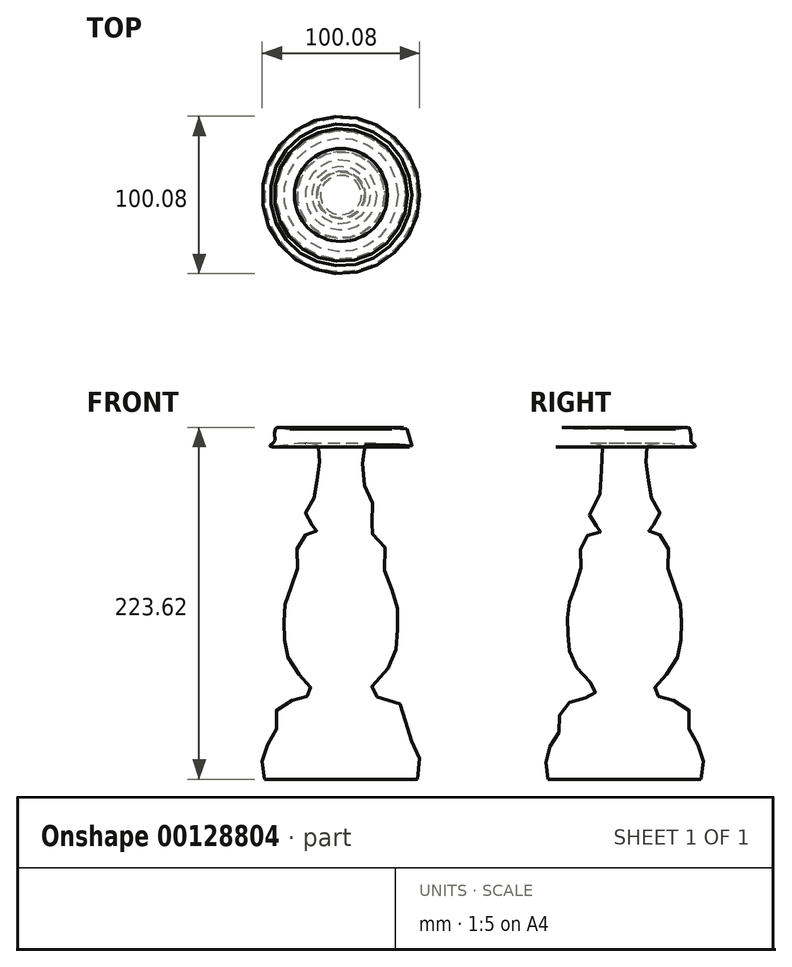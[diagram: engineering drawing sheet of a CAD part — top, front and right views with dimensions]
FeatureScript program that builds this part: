
annotation { "Feature Type Name" : "Feature", "Feature Type Description" : "" }
export const myFeature = defineFeature(function(context is Context, id is Id, definition is map)
    precondition{}
    {
        {
            var Q0;
            Q0=qCreatedBy(makeId("Top.planeOp"),FACE);
            cPlane(context, id + "F0", {"entities" : qUnion([Q0]), "cplaneType" : CPlaneType.OFFSET, "offset" : 19 * mm, "width" : 150 * mm, "height" : 150 * mm});
        }
        {
            var Q0;
            Q0=qCreatedBy(id+"F0.planeOp",FACE);
            cPlane(context, id + "F1", {"entities" : qUnion([Q0]), "cplaneType" : CPlaneType.OFFSET, "offset" : 3 * mm, "width" : 150 * mm, "height" : 150 * mm});
        }
        {
            var Q0;
            Q0=qCreatedBy(id+"F1.planeOp",FACE);
            cPlane(context, id + "F2", {"entities" : qUnion([Q0]), "cplaneType" : CPlaneType.OFFSET, "offset" : 5 * mm, "width" : 150 * mm, "height" : 150 * mm});
        }
        {
            var Q0;
            Q0=qCreatedBy(id+"F2.planeOp",FACE);
            cPlane(context, id + "F3", {"entities" : qUnion([Q0]), "cplaneType" : CPlaneType.OFFSET, "offset" : 5 * mm, "width" : 150 * mm, "height" : 150 * mm});
        }
        {
            var Q0;
            Q0=qCreatedBy(id+"F3.planeOp",FACE);
            cPlane(context, id + "F4", {"entities" : qUnion([Q0]), "cplaneType" : CPlaneType.OFFSET, "offset" : 13 * mm, "width" : 150 * mm, "height" : 150 * mm});
        }
        {
            var Q0;
            Q0=qCreatedBy(id+"F4.planeOp",FACE);
            cPlane(context, id + "F5", {"entities" : qUnion([Q0]), "cplaneType" : CPlaneType.OFFSET, "offset" : 10 * mm, "width" : 150 * mm, "height" : 150 * mm});
        }
        {
            var Q0;
            Q0=qCreatedBy(id+"F5.planeOp",FACE);
            cPlane(context, id + "F6", {"entities" : qUnion([Q0]), "cplaneType" : CPlaneType.OFFSET, "offset" : 15 * mm, "width" : 150 * mm, "height" : 150 * mm});
        }
        {
            var Q0;
            Q0=qCreatedBy(id+"F6.planeOp",FACE);
            cPlane(context, id + "F7", {"entities" : qUnion([Q0]), "cplaneType" : CPlaneType.OFFSET, "offset" : 25 * mm, "width" : 150 * mm, "height" : 150 * mm});
        }
        {
            var Q0;
            Q0=qCreatedBy(id+"F7.planeOp",FACE);
            cPlane(context, id + "F8", {"entities" : qUnion([Q0]), "cplaneType" : CPlaneType.OFFSET, "offset" : 20 * mm, "width" : 150 * mm, "height" : 150 * mm});
        }
        {
            var Q0;
            Q0=qCreatedBy(id+"F8.planeOp",FACE);
            cPlane(context, id + "F9", {"entities" : qUnion([Q0]), "cplaneType" : CPlaneType.OFFSET, "offset" : 20 * mm, "width" : 150 * mm, "height" : 150 * mm});
        }
        {
            var Q0;
            Q0=qCreatedBy(id+"F9.planeOp",FACE);
            cPlane(context, id + "F10", {"entities" : qUnion([Q0]), "cplaneType" : CPlaneType.OFFSET, "offset" : 20 * mm, "width" : 150 * mm, "height" : 150 * mm});
        }
        {
            var Q0;
            Q0=qCreatedBy(id+"F10.planeOp",FACE);
            cPlane(context, id + "F11", {"entities" : qUnion([Q0]), "cplaneType" : CPlaneType.OFFSET, "offset" : 2 * mm, "width" : 150 * mm, "height" : 150 * mm});
        }
        {
            var Q0;
            Q0=qCreatedBy(id+"F11.planeOp",FACE);
            cPlane(context, id + "F12", {"entities" : qUnion([Q0]), "cplaneType" : CPlaneType.OFFSET, "offset" : 8.5 * mm, "width" : 150 * mm, "height" : 150 * mm});
        }
        {
            var Q0;
            Q0=qCreatedBy(id+"F12.planeOp",FACE);
            cPlane(context, id + "F13", {"entities" : qUnion([Q0]), "cplaneType" : CPlaneType.OFFSET, "offset" : 8.5 * mm, "width" : 150 * mm, "height" : 150 * mm});
        }
        {
            var Q0;
            Q0=qCreatedBy(id+"F13.planeOp",FACE);
            cPlane(context, id + "F14", {"entities" : qUnion([Q0]), "cplaneType" : CPlaneType.OFFSET, "offset" : 8.5 * mm, "width" : 150 * mm, "height" : 150 * mm});
        }
        {
            var Q0;
            Q0=qCreatedBy(id+"F14.planeOp",FACE);
            cPlane(context, id + "F15", {"entities" : qUnion([Q0]), "cplaneType" : CPlaneType.OFFSET, "offset" : 8.5 * mm, "width" : 150 * mm, "height" : 150 * mm});
        }
        {
            var Q0;
            Q0=qCreatedBy(id+"F15.planeOp",FACE);
            cPlane(context, id + "F16", {"entities" : qUnion([Q0]), "cplaneType" : CPlaneType.OFFSET, "offset" : 1 * mm, "width" : 150 * mm, "height" : 150 * mm});
        }
        {
            var Q0;
            Q0=qCreatedBy(id+"F16.planeOp",FACE);
            cPlane(context, id + "F17", {"entities" : qUnion([Q0]), "cplaneType" : CPlaneType.OFFSET, "offset" : 20 * mm, "width" : 150 * mm, "height" : 150 * mm});
        }
        {
            var Q0;
            Q0=qCreatedBy(id+"F17.planeOp",FACE);
            cPlane(context, id + "F18", {"entities" : qUnion([Q0]), "cplaneType" : CPlaneType.OFFSET, "offset" : 1 * mm, "width" : 150 * mm, "height" : 150 * mm});
        }
        {
            var Q0;
            Q0=qCreatedBy(id+"F18.planeOp",FACE);
            cPlane(context, id + "F19", {"entities" : qUnion([Q0]), "cplaneType" : CPlaneType.OFFSET, "offset" : 2 * mm, "width" : 150 * mm, "height" : 150 * mm});
        }
        {
            var Q0;
            Q0=qCreatedBy(id+"F19.planeOp",FACE);
            cPlane(context, id + "F20", {"entities" : qUnion([Q0]), "cplaneType" : CPlaneType.OFFSET, "offset" : 3 * mm, "width" : 150 * mm, "height" : 150 * mm});
        }
        {
            var Q0;
            Q0=qCreatedBy(id+"F20.planeOp",FACE);
            cPlane(context, id + "F21", {"entities" : qUnion([Q0]), "cplaneType" : CPlaneType.OFFSET, "offset" : 2 * mm, "width" : 150 * mm, "height" : 150 * mm});
        }
        {
            var Q0;
            Q0=qCreatedBy(id+"F21.planeOp",FACE);
            cPlane(context, id + "F22", {"entities" : qUnion([Q0]), "cplaneType" : CPlaneType.OFFSET, "offset" : 3 * mm, "width" : 150 * mm, "height" : 150 * mm});
        }
        {
            var Q0;
            Q0=qCreatedBy(id+"F22.planeOp",FACE);
            cPlane(context, id + "F23", {"entities" : qUnion([Q0]), "cplaneType" : CPlaneType.OFFSET, "offset" : 0.4 * mm, "width" : 150 * mm, "height" : 150 * mm});
        }
        {
            var Q0;
            Q0=qCreatedBy(makeId("Top.planeOp"),FACE);
            var sketch = newSketch(context, id + "F24", { "sketchPlane" : qUnion([Q0])});
            skCircle(sketch, "E0", {"center": v(0, 0) * mm, "radius": 48.5 * mm});
            skSolve(sketch);
        }
        {
            var Q0;
            Q0=qCreatedBy(id+"F0.planeOp",FACE);
            var sketch = newSketch(context, id + "F25", { "sketchPlane" : qUnion([Q0])});
            skCircle(sketch, "E1", {"center": v(0, 0) * mm, "radius": 48.5 * mm});
            skSolve(sketch);
        }
        {
            var Q0;
            Q0=qCreatedBy(id+"F2.planeOp",FACE);
            var sketch = newSketch(context, id + "F26", { "sketchPlane" : qUnion([Q0])});
            skCircle(sketch, "E2", {"center": v(0, 0) * mm, "radius": 43 * mm});
            skSolve(sketch);
        }
        {
            var Q0;
            Q0=qCreatedBy(id+"F3.planeOp",FACE);
            var sketch = newSketch(context, id + "F27", { "sketchPlane" : qUnion([Q0])});
            skCircle(sketch, "E3", {"center": v(0, 0) * mm, "radius": 41 * mm});
            skSolve(sketch);
        }
        {
            var Q0;
            Q0=qCreatedBy(id+"F4.planeOp",FACE);
            var sketch = newSketch(context, id + "F28", { "sketchPlane" : qUnion([Q0])});
            skCircle(sketch, "E4", {"center": v(0, 0) * mm, "radius": 40.5 * mm});
            skSolve(sketch);
        }
        {
            var Q0;
            Q0=qCreatedBy(id+"F5.planeOp",FACE);
            var sketch = newSketch(context, id + "F29", { "sketchPlane" : qUnion([Q0])});
            skCircle(sketch, "E5", {"center": v(0, 0) * mm, "radius": 18.5 * mm});
            skSolve(sketch);
        }
        {
            var Q0;
            Q0=qCreatedBy(id+"F6.planeOp",FACE);
            var sketch = newSketch(context, id + "F30", { "sketchPlane" : qUnion([Q0])});
            skCircle(sketch, "E6", {"center": v(0, 0) * mm, "radius": 29.5 * mm});
            skSolve(sketch);
        }
        {
            var Q0;
            Q0=qCreatedBy(id+"F7.planeOp",FACE);
            var sketch = newSketch(context, id + "F31", { "sketchPlane" : qUnion([Q0])});
            skCircle(sketch, "E7", {"center": v(0, 0) * mm, "radius": 36 * mm});
            skSolve(sketch);
        }
        {
            var Q0;
            Q0=qCreatedBy(id+"F8.planeOp",FACE);
            var sketch = newSketch(context, id + "F32", { "sketchPlane" : qUnion([Q0])});
            skCircle(sketch, "E8", {"center": v(0, 0) * mm, "radius": 34.5 * mm});
            skSolve(sketch);
        }
        {
            var Q0;
            Q0=qCreatedBy(id+"F9.planeOp",FACE);
            var sketch = newSketch(context, id + "F33", { "sketchPlane" : qUnion([Q0])});
            skCircle(sketch, "E9", {"center": v(0, 0) * mm, "radius": 27.5 * mm});
            skSolve(sketch);
        }
        {
            var Q0;
            Q0=qCreatedBy(id+"F10.planeOp",FACE);
            var sketch = newSketch(context, id + "F34", { "sketchPlane" : qUnion([Q0])});
            skCircle(sketch, "E10", {"center": v(0, 0) * mm, "radius": 23.5 * mm});
            skSolve(sketch);
        }
        {
            var Q0;
            Q0=qCreatedBy(id+"F11.planeOp",FACE);
            var sketch = newSketch(context, id + "F35", { "sketchPlane" : qUnion([Q0])});
            skCircle(sketch, "E11", {"center": v(0, 0) * mm, "radius": 15.5 * mm});
            skSolve(sketch);
        }
        {
            var Q0;
            Q0=qCreatedBy(id+"F12.planeOp",FACE);
            var sketch = newSketch(context, id + "F36", { "sketchPlane" : qUnion([Q0])});
            skCircle(sketch, "E12", {"center": v(0, 0) * mm, "radius": 21.5 * mm});
            skSolve(sketch);
        }
        {
            var Q0;
            Q0=qCreatedBy(id+"F13.planeOp",FACE);
            var sketch = newSketch(context, id + "F37", { "sketchPlane" : qUnion([Q0])});
            skCircle(sketch, "E13", {"center": v(0, 0) * mm, "radius": 21.04 * mm});
            skSolve(sketch);
        }
        {
            var Q0;
            Q0=qCreatedBy(id+"F14.planeOp",FACE);
            var sketch = newSketch(context, id + "F38", { "sketchPlane" : qUnion([Q0])});
            skCircle(sketch, "E14", {"center": v(0, 0) * mm, "radius": 15 * mm});
            skSolve(sketch);
        }
        {
            var Q0;
            Q0=qCreatedBy(id+"F15.planeOp",FACE);
            var sketch = newSketch(context, id + "F39", { "sketchPlane" : qUnion([Q0])});
            skCircle(sketch, "E15", {"center": v(0, 0) * mm, "radius": 15.25 * mm});
            skSolve(sketch);
        }
        {
            var Q0;
            Q0=qCreatedBy(id+"F16.planeOp",FACE);
            var sketch = newSketch(context, id + "F40", { "sketchPlane" : qUnion([Q0])});
            skCircle(sketch, "E16", {"center": v(0, 0) * mm, "radius": 15.25 * mm});
            skSolve(sketch);
        }
        {
            var Q0;
            Q0=qCreatedBy(id+"F17.planeOp",FACE);
            var sketch = newSketch(context, id + "F41", { "sketchPlane" : qUnion([Q0])});
            skCircle(sketch, "E17", {"center": v(0, 0) * mm, "radius": 15 * mm});
            skSolve(sketch);
        }
        {
            var Q0;
            Q0=qCreatedBy(id+"F18.planeOp",FACE);
            var sketch = newSketch(context, id + "F42", { "sketchPlane" : qUnion([Q0])});
            skCircle(sketch, "E18", {"center": v(0, 0) * mm, "radius": 44 * mm});
            skSolve(sketch);
        }
        {
            var Q0;
            Q0=qCreatedBy(id+"F19.planeOp",FACE);
            var sketch = newSketch(context, id + "F43", { "sketchPlane" : qUnion([Q0])});
            skCircle(sketch, "E19", {"center": v(0, 0) * mm, "radius": 42 * mm});
            skSolve(sketch);
        }
        {
            var Q0;
            Q0=qCreatedBy(id+"F20.planeOp",FACE);
            var sketch = newSketch(context, id + "F44", { "sketchPlane" : qUnion([Q0])});
            skCircle(sketch, "E20", {"center": v(0, 0) * mm, "radius": 42 * mm});
            skSolve(sketch);
        }
        {
            var Q0;
            Q0=qCreatedBy(id+"F22.planeOp",FACE);
            var sketch = newSketch(context, id + "F45", { "sketchPlane" : qUnion([Q0])});
            skCircle(sketch, "E21", {"center": v(0, 0) * mm, "radius": 41.5 * mm});
            skSolve(sketch);
        }
        {
            var Q0;
            Q0=qCreatedBy(id+"F22.planeOp",FACE);
            var sketch = newSketch(context, id + "F46", { "sketchPlane" : qUnion([Q0])});
            skCircle(sketch, "E22", {"center": v(0, 0) * mm, "radius": 30 * mm});
            skSolve(sketch);
        }
        {
            var Q0;
            Q0=qCreatedBy(id+"F23.planeOp",FACE);
            var sketch = newSketch(context, id + "F47", { "sketchPlane" : qUnion([Q0])});
            skCircle(sketch, "E23", {"center": v(0, 0) * mm, "radius": 29.5 * mm});
            skSolve(sketch);
        }
        {
            var Q0;
            Q0 = qSketchRegion(id + "F24", true);
            var Q1;
            Q1 = qSketchRegion(id + "F25", true);
            var Q2;
            Q2 = qSketchRegion(id + "F26", true);
            var Q3;
            Q3 = qSketchRegion(id + "F27", true);
            var Q4;
            Q4 = qSketchRegion(id + "F28", true);
            var Q5;
            Q5 = qSketchRegion(id + "F29", true);
            var Q6;
            Q6 = qSketchRegion(id + "F30", true);
            var Q7;
            Q7 = qSketchRegion(id + "F31", true);
            var Q8;
            Q8 = qSketchRegion(id + "F32", true);
            var Q9;
            Q9 = qSketchRegion(id + "F33", true);
            var Q10;
            Q10 = qSketchRegion(id + "F34", true);
            var Q11;
            Q11 = qSketchRegion(id + "F35", true);
            var Q12;
            Q12 = qSketchRegion(id + "F36", true);
            var Q13;
            Q13 = qSketchRegion(id + "F37", true);
            var Q14;
            Q14 = qSketchRegion(id + "F38", true);
            var Q15;
            Q15 = qSketchRegion(id + "F39", true);
            var Q16;
            Q16 = qSketchRegion(id + "F40", true);
            var Q17;
            Q17 = qSketchRegion(id + "F41", true);
            var Q18;
            Q18 = qSketchRegion(id + "F42", true);
            var Q19;
            Q19 = qSketchRegion(id + "F43", true);
            var Q20;
            Q20 = qSketchRegion(id + "F44", true);
            var Q21;
            Q21 = qSketchRegion(id + "F45", true);
            var Q22;
            Q22 = qSketchRegion(id + "F46", true);
            var Q23;
            Q23 = qSketchRegion(id + "F47", true);
            loft(context, id + "F48", {"sheetProfilesArray" : [{ "sheetProfileEntities" : qUnion([Q0]) }, { "sheetProfileEntities" : qUnion([Q1]) }, { "sheetProfileEntities" : qUnion([Q2]) }, { "sheetProfileEntities" : qUnion([Q3]) }, { "sheetProfileEntities" : qUnion([Q4]) }, { "sheetProfileEntities" : qUnion([Q5]) }, { "sheetProfileEntities" : qUnion([Q6]) }, { "sheetProfileEntities" : qUnion([Q7]) }, { "sheetProfileEntities" : qUnion([Q8]) }, { "sheetProfileEntities" : qUnion([Q9]) }, { "sheetProfileEntities" : qUnion([Q10]) }, { "sheetProfileEntities" : qUnion([Q11]) }, { "sheetProfileEntities" : qUnion([Q12]) }, { "sheetProfileEntities" : qUnion([Q13]) }, { "sheetProfileEntities" : qUnion([Q14]) }, { "sheetProfileEntities" : qUnion([Q15]) }, { "sheetProfileEntities" : qUnion([Q16]) }, { "sheetProfileEntities" : qUnion([Q17]) }, { "sheetProfileEntities" : qUnion([Q18]) }, { "sheetProfileEntities" : qUnion([Q19]) }, { "sheetProfileEntities" : qUnion([Q20]) }, { "sheetProfileEntities" : qUnion([Q21]) }, { "sheetProfileEntities" : qUnion([Q22]) }, { "sheetProfileEntities" : qUnion([Q23]) }]});
        }
    });
